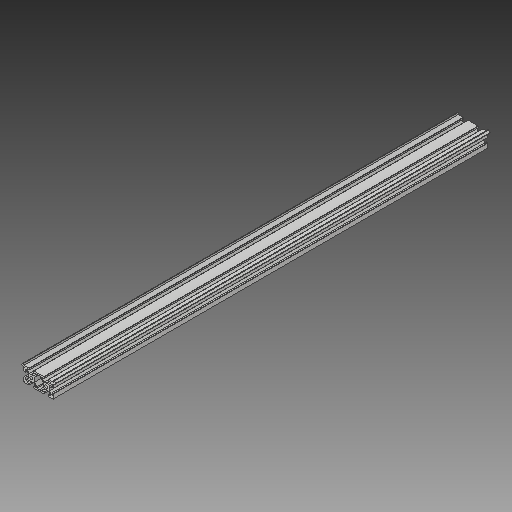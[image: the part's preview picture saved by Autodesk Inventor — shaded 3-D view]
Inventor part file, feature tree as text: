
AUTODESK INVENTOR PART (.ipt)
format: ipt  version: 2018 (Build 220112000, 112)  size: 287,232 bytes
history: native  units: mm
features: other x3, sketch x1
ambient origin geometry x8: Origin, YZ Plane, XZ Plane, XY Plane, X Axis, Y Axis, Z Axis, Center Point
bodies: Solid1 (feature_tree)
feature tree (4):
  other  "Makerslide 580mm.ipt"
  other  "Solid1::Makerslide 580mm.ipt"
  other  "TaggingFeature1"
  sketch  "Sketch1"  dims[d0=10.0mm]
